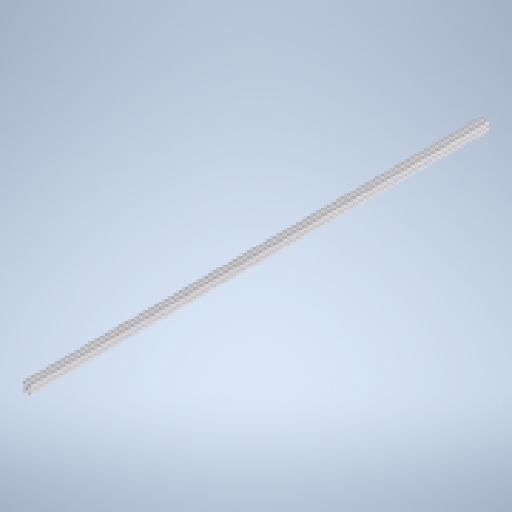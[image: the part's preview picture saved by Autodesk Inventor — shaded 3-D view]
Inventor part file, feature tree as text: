
AUTODESK INVENTOR PART (.ipt)
format: ipt  version: 2025 (Build 290162010, 162A)  size: 236,544 bytes
history: native  units: mm
features: thread x2, chamfer x2, other x1
ambient origin geometry x8: Origin, YZ Plane, XZ Plane, XY Plane, X Axis, Y Axis, Z Axis, Center Point
bodies: Volumenkörper1 (feature_tree)
feature tree (5):
  thread  "Gewinde1"  [1 undecoded]
  chamfer  "Fasen1"  Distance=2.0mm Angle=45.0deg
  thread  "Gewinde2"  [1 undecoded]
  chamfer  "Fasen2"  Distance=2.0mm Angle=45.0deg
  other  "item_37003_profil-5-20x20-natur-370_1096_high_1_1:1"
note: 2 required parameter values undecoded (feature->parameter linkage not recoverable at this tier; creation-order binding heuristic only, values carry confidence <= 0.55)
